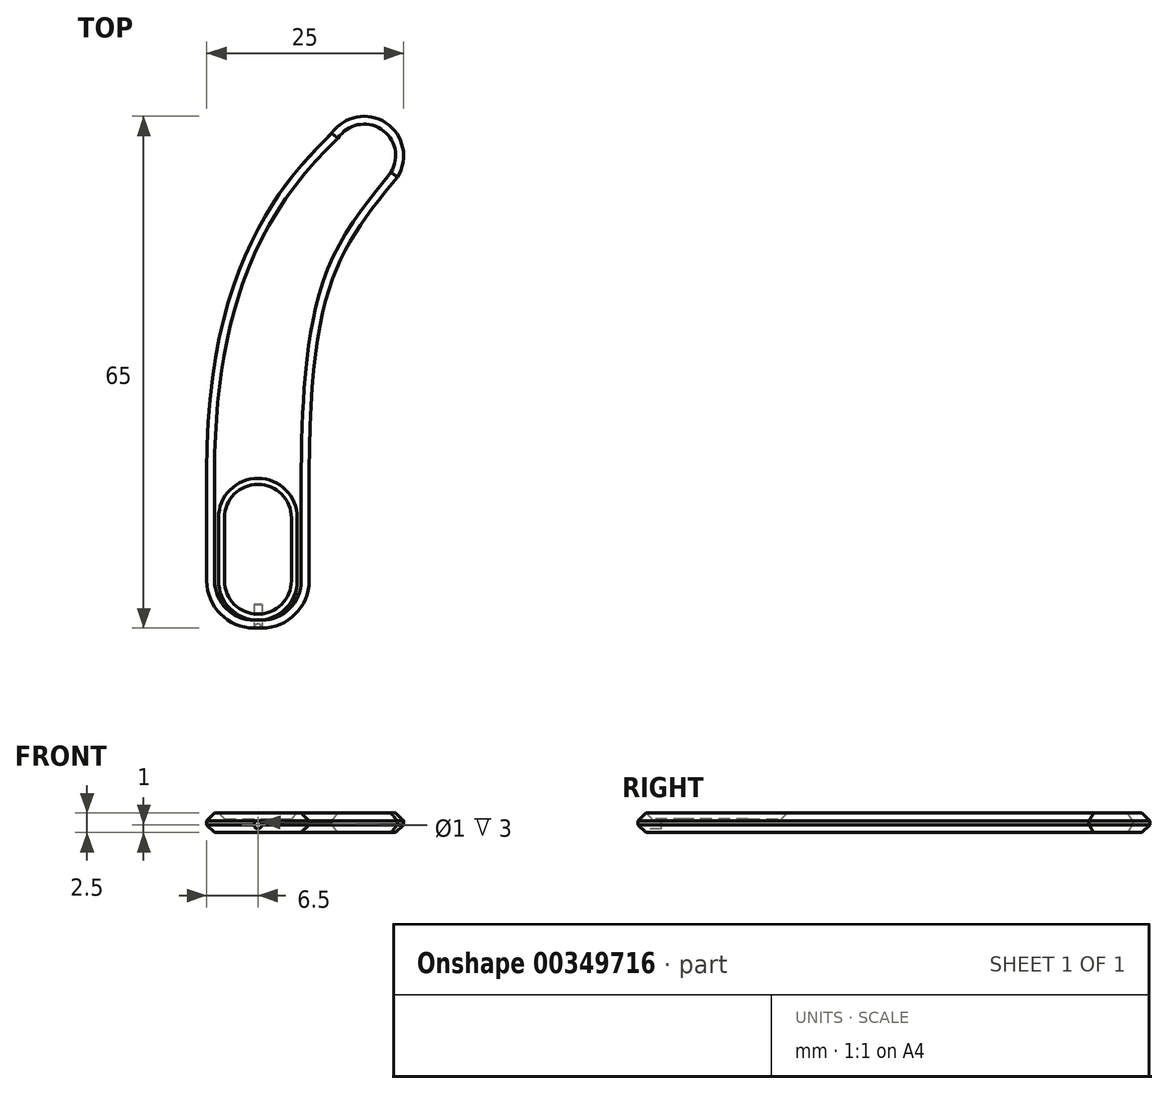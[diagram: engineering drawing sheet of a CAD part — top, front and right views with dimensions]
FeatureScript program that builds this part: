
annotation { "Feature Type Name" : "Feature", "Feature Type Description" : "" }
export const myFeature = defineFeature(function(context is Context, id is Id, definition is map)
    precondition{}
    {
        {
            var Q0;
            Q0=qCreatedBy(makeId("Top.planeOp"),FACE);
            var sketch = newSketch(context, id + "F0", { "sketchPlane" : qUnion([Q0])});
            skLineSegment(sketch, "E0", {"start": v(0, 0) * mm, "end": v(0, 20) * mm});
            skLineSegment(sketch, "E1", {"start": v(0, 0) * mm, "end": v(13, 0) * mm});
            skLineSegment(sketch, "E2", {"start": v(13, 0) * mm, "end": v(13, 20) * mm});
            skCircle(sketch, "E3", {"center": v(20, 60) * mm, "radius": 5 * mm});
            skFitSpline(sketch, "E4", {"points": [v(0, 20) * mm, v(15.9, 62.85) * mm], "startDerivative": vector(0, 74.48) * mm, "endDerivative": vector(21.48, 20.68) * mm});
            skFitSpline(sketch, "E5", {"points": [v(13, 20) * mm, v(24.2, 57.3) * mm], "startDerivative": vector(0.52, 71.8) * mm, "endDerivative": vector(22.13, 27.66) * mm});
            skSolve(sketch);
        }
        {
            var Q0;
            Q0=makeQuery(id+"F0.imprint","IMPRINT",FACE,{"disambiguationData":[TD([[makeQuery(id+"F0.imprint","IMPRINT",EDGE,{"derivedFrom":sQuery(id+"F0.wireOp",EDGE,"E0")}),-1.0]])]});
            var Q1;
            {var subQ0=sQuery(id+"F0.wireOp",EDGE,"E3");var subQ1=makeQuery(id+"F0.imprint","INTERSECT",VERTEX,{"derivedFrom":[subQ0,sQuery(id+"F0.wireOp",EDGE,"E4")]});Q1=makeQuery(id+"F0.imprint","IMPRINT",FACE,{"disambiguationData":[TD([[makeQuery(id+"F0.imprint","IMPRINT",EDGE,{"disambiguationData":[TD([[subQ1,-1.0]])],"derivedFrom":subQ0}),1.0]])]});}
            extrude(context, id + "F1", {"entities" : qUnion([Q0, Q1]), "depth" : 2.5 * mm, "offsetDistance" : 25 * mm});
        }
        {
            var Q0;
            Q0=makeQuery(id+"F1.opExtrude","CAP_FACE",FACE,{"disambiguationData":[OSD([sQuery(id+"F0.wireOp",EDGE,"E0"),sQuery(id+"F0.wireOp",EDGE,"E1"),sQuery(id+"F0.wireOp",EDGE,"E2"),sQuery(id+"F0.wireOp",EDGE,"E3"),sQuery(id+"F0.wireOp",EDGE,"E4"),sQuery(id+"F0.wireOp",EDGE,"E5")])],"isStart":false});
            var sketch = newSketch(context, id + "F2", { "sketchPlane" : qUnion([Q0])});
            skFitSpline(sketch, "E6.0", {"points": [v(0, 20) * mm, v(0, 44.83) * mm, v(9.48, 61.8) * mm, v(16.63, 68.7) * mm]});
            skLineSegment(sketch, "E6.1", {"start": v(0, 0) * mm, "end": v(0, 20) * mm});
            skLineSegment(sketch, "E6.2", {"start": v(0, 0) * mm, "end": v(13, 0) * mm});
            skLineSegment(sketch, "E6.3", {"start": v(13, 0) * mm, "end": v(13, 20) * mm});
            skFitSpline(sketch, "E6.4", {"points": [v(13, 20) * mm, v(13.17, 43.93) * mm, v(16.8, 53.04) * mm, v(24.19, 62.26) * mm]});
            skArc(sketch, "E6.5", {"start": v(24.2, 57.3) * mm, "mid": v(22.77, 64.16) * mm, "end": v(15.9, 62.85) * mm});
            skPoint(sketch, "E7", {"position": v(6.5, 10) * mm});
            skPoint(sketch, "E7.positionSnap0", {"position": v(0, 10) * mm});
            skPoint(sketch, "E7.positionSnap1", {"position": v(6.5, 0) * mm});
            skLineSegment(sketch, "E8.bottom", {"start": v(2.5, 14) * mm, "end": v(10.5, 14) * mm});
            skLineSegment(sketch, "E8.top", {"start": v(2.5, 6) * mm, "end": v(10.5, 6) * mm});
            skLineSegment(sketch, "E8.left", {"start": v(2.5, 14) * mm, "end": v(2.5, 6) * mm});
            skLineSegment(sketch, "E8.right", {"start": v(10.5, 14) * mm, "end": v(10.5, 6) * mm});
            skArc(sketch, "E9", {"start": v(2.5, 14) * mm, "mid": v(6.5, 18) * mm, "end": v(10.5, 14) * mm});
            skArc(sketch, "E10", {"start": v(2.5, 6) * mm, "mid": v(6.5, 2) * mm, "end": v(10.5, 6) * mm});
            skSolve(sketch);
        }
        {
            var Q0;
            Q0=makeQuery(id+"F2.imprint","IMPRINT",FACE,{"disambiguationData":[TD([[makeQuery(id+"F2.imprint","IMPRINT",EDGE,{"derivedFrom":sQuery(id+"F2.wireOp",EDGE,"E8.bottom")}),1.0]])]});
            var Q1;
            Q1=makeQuery(id+"F2.imprint","IMPRINT",FACE,{"disambiguationData":[TD([[makeQuery(id+"F2.imprint","IMPRINT",EDGE,{"derivedFrom":sQuery(id+"F2.wireOp",EDGE,"E8.bottom")}),-1.0]])]});
            var Q2;
            Q2=makeQuery(id+"F2.imprint","IMPRINT",FACE,{"disambiguationData":[TD([[makeQuery(id+"F2.imprint","IMPRINT",EDGE,{"derivedFrom":sQuery(id+"F2.wireOp",EDGE,"E8.top")}),-1.0]])]});
            extrude(context, id + "F3", {"entities" : qUnion([Q0, Q1, Q2]), "operationType" : NewBodyOperationType.REMOVE, "oppositeDirection" : true, "depth" : .75 * mm, "offsetDistance" : 25 * mm});
        }
        {
            var Q0;
            Q0=makeQuery(id+"F1.opExtrude","SWEPT_EDGE",EDGE,{"disambiguationData":[OSD([sQuery(id+"F0.wireOp",EDGE,"E1"),sQuery(id+"F0.wireOp",EDGE,"E2")])]});
            var Q1;
            Q1=makeQuery(id+"F1.opExtrude","SWEPT_EDGE",EDGE,{"disambiguationData":[OSD([sQuery(id+"F0.wireOp",EDGE,"E0"),sQuery(id+"F0.wireOp",EDGE,"E1")])]});
            fillet(context, id + "F4", {"entities" : qUnion([Q0, Q1]), "radius" : 6 * mm, "tangentPropagation" : true, "allowEdgeOverflow" : false});
        }
        {
            var Q0;
            Q0=makeQuery(id+"F1.opExtrude","CAP_EDGE",EDGE,{"disambiguationData":[OSD([sQuery(id+"F0.wireOp",EDGE,"E1")])],"isStart":true});
            var Q1;
            Q1=makeQuery(id+"F1.opExtrude","CAP_EDGE",EDGE,{"disambiguationData":[OSD([sQuery(id+"F0.wireOp",EDGE,"E2")])],"isStart":true});
            var Q2;
            Q2=makeQuery(id+"F1.opExtrude","CAP_EDGE",EDGE,{"disambiguationData":[OSD([sQuery(id+"F0.wireOp",EDGE,"E5")])],"isStart":true});
            var Q3;
            Q3=makeQuery(id+"F1.opExtrude","CAP_EDGE",EDGE,{"disambiguationData":[OSD([sQuery(id+"F0.wireOp",EDGE,"E3")])],"isStart":true});
            var Q4;
            Q4=makeQuery(id+"F1.opExtrude","CAP_EDGE",EDGE,{"disambiguationData":[OSD([sQuery(id+"F0.wireOp",EDGE,"E4")])],"isStart":true});
            var Q5;
            Q5=makeQuery(id+"F1.opExtrude","CAP_EDGE",EDGE,{"disambiguationData":[OSD([sQuery(id+"F0.wireOp",EDGE,"E0")])],"isStart":true});
            chamfer(context, id + "F5", {"entities" : qUnion([Q0, Q1, Q2, Q3, Q4, Q5]), "width" : 1 * mm, "tangentPropagation" : true});
        }
        {
            var Q0;
            Q0=makeQuery(id+"F1.opExtrude","CAP_EDGE",EDGE,{"disambiguationData":[OSD([sQuery(id+"F0.wireOp",EDGE,"E5")])],"isStart":false});
            var Q1;
            Q1=makeQuery(id+"F1.opExtrude","CAP_EDGE",EDGE,{"disambiguationData":[OSD([sQuery(id+"F0.wireOp",EDGE,"E3")])],"isStart":false});
            var Q2;
            Q2=makeQuery(id+"F1.opExtrude","CAP_EDGE",EDGE,{"disambiguationData":[OSD([sQuery(id+"F0.wireOp",EDGE,"E4")])],"isStart":false});
            var Q3;
            Q3=makeQuery(id+"F1.opExtrude","CAP_EDGE",EDGE,{"disambiguationData":[OSD([sQuery(id+"F0.wireOp",EDGE,"E0")])],"isStart":false});
            var Q4;
            Q4=makeQuery(id+"F1.opExtrude","CAP_EDGE",EDGE,{"disambiguationData":[OSD([sQuery(id+"F0.wireOp",EDGE,"E2")])],"isStart":false});
            var Q5;
            Q5=makeQuery(id+"F1.opExtrude","CAP_EDGE",EDGE,{"disambiguationData":[OSD([sQuery(id+"F0.wireOp",EDGE,"E1")])],"isStart":false});
            var Q6;
            Q6=makeQuery(id+"F1.opExtrude","CAP_FACE",FACE,{"disambiguationData":[OSD([sQuery(id+"F0.wireOp",EDGE,"E0"),sQuery(id+"F0.wireOp",EDGE,"E1"),sQuery(id+"F0.wireOp",EDGE,"E2"),sQuery(id+"F0.wireOp",EDGE,"E3"),sQuery(id+"F0.wireOp",EDGE,"E4"),sQuery(id+"F0.wireOp",EDGE,"E5")])],"isStart":false});
            chamfer(context, id + "F6", {"entities" : qUnion([Q0, Q1, Q2, Q3, Q4, Q5, Q6]), "width" : 1 * mm, "tangentPropagation" : true});
        }
        {
            var Q0;
            Q0=makeQuery(id+"F1.opExtrude","SWEPT_FACE",FACE,{"disambiguationData":[OSD([sQuery(id+"F0.wireOp",EDGE,"E1")])]});
            cPlane(context, id + "F7", {"entities" : qUnion([Q0]), "cplaneType" : CPlaneType.OFFSET, "offset" : 0 * mm, "width" : 150 * mm, "height" : 150 * mm});
        }
        {
            var Q0;
            Q0=qCreatedBy(id+"F7.planeOp",FACE);
            var sketch = newSketch(context, id + "F8", { "sketchPlane" : qUnion([Q0])});
            skCircle(sketch, "E11", {"center": v(6.5, 1) * mm, "radius": 0.5 * mm});
            skLineSegment(sketch, "E12.0", {"start": v(6, 0) * mm, "end": v(1, 0) * mm});
            skLineSegment(sketch, "E12.1", {"start": v(7, 0) * mm, "end": v(6, 0) * mm});
            skLineSegment(sketch, "E12.2", {"start": v(12, 0) * mm, "end": v(7, 0) * mm});
            skLineSegment(sketch, "E13.0", {"start": v(0, 1) * mm, "end": v(0, 1.5) * mm});
            skLineSegment(sketch, "E14", {"start": v(0, 1) * mm, "end": v(0, 0) * mm});
            skSolve(sketch);
        }
        {
            var Q0;
            Q0=makeQuery(id+"F8.imprint","IMPRINT",FACE,{"disambiguationData":[TD([[makeQuery(id+"F8.imprint","IMPRINT",EDGE,{"derivedFrom":sQuery(id+"F8.wireOp",EDGE,"E11")}),1.0]])]});
            extrude(context, id + "F9", {"entities" : qUnion([Q0]), "operationType" : NewBodyOperationType.REMOVE, "oppositeDirection" : true, "depth" : 3 * mm, "offsetDistance" : 25 * mm});
        }
    });
